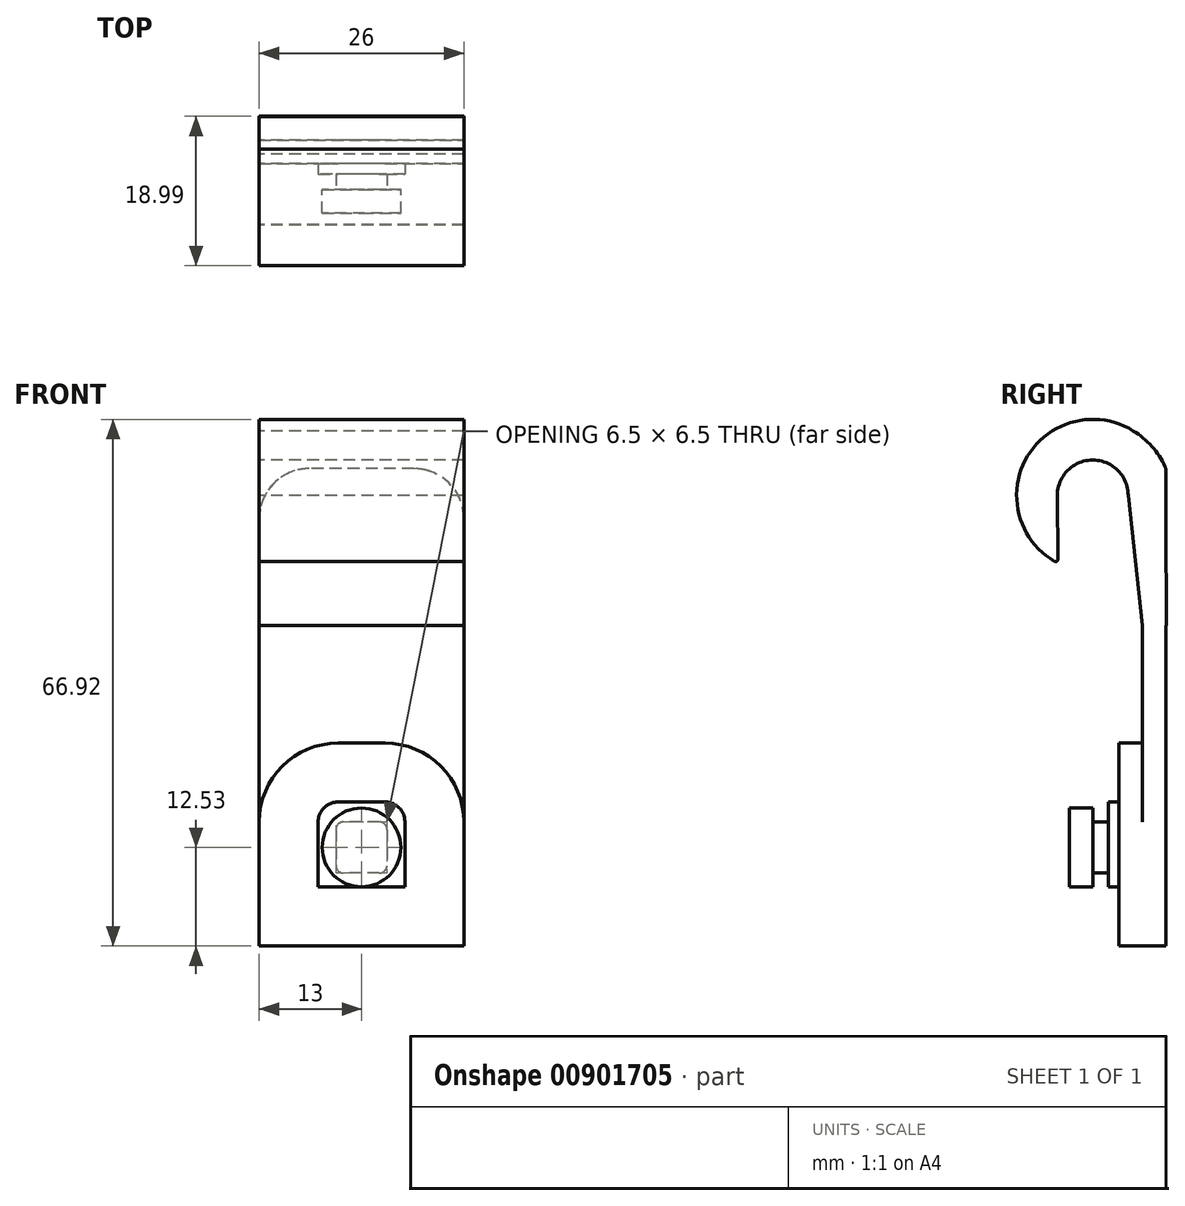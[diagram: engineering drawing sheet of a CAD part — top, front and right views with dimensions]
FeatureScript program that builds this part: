
annotation { "Feature Type Name" : "Feature", "Feature Type Description" : "" }
export const myFeature = defineFeature(function(context is Context, id is Id, definition is map)
    precondition{}
    {
        {
            var Q0;
            Q0=qCreatedBy(makeId("Front.planeOp"),FACE);
            var sketch = newSketch(context, id + "F0", { "sketchPlane" : qUnion([Q0])});
            skCircle(sketch, "E0", {"center": v(0, 0) * mm, "radius": 5 * mm});
            skSolve(sketch);
        }
        {
            var Q0;
            Q0 = qSketchRegion(id + "F0", true);
            extrude(context, id + "F1", {"entities" : qUnion([Q0]), "depth" : 3 * mm, "offsetDistance" : 25.4 * mm});
        }
        {
            var Q0;
            Q0=qCreatedBy(makeId("Front.planeOp"),FACE);
            var sketch = newSketch(context, id + "F2", { "sketchPlane" : qUnion([Q0])});
            skLineSegment(sketch, "E1.bottom", {"start": v(2.25, 3.25) * mm, "end": v(-2.25, 3.25) * mm});
            skLineSegment(sketch, "E1.top", {"start": v(2.25, -3.25) * mm, "end": v(-2.25, -3.25) * mm});
            skLineSegment(sketch, "E1.left", {"start": v(3.25, 2.25) * mm, "end": v(3.25, -2.25) * mm});
            skLineSegment(sketch, "E1.right", {"start": v(-3.25, 2.25) * mm, "end": v(-3.25, -2.25) * mm});
            skPoint(sketch, "E1.middle", {"position": v(0, 0) * mm});
            skArc(sketch, "E2", {"start": v(-2.25, 3.25) * mm, "mid": v(-2.96, 2.96) * mm, "end": v(-3.25, 2.25) * mm});
            skArc(sketch, "E3.MirrorCS", {"start": v(2.25, 3.25) * mm, "mid": v(2.96, 2.96) * mm, "end": v(3.25, 2.25) * mm});
            skArc(sketch, "E4.MirrorCS", {"start": v(-2.25, -3.25) * mm, "mid": v(-2.96, -2.96) * mm, "end": v(-3.25, -2.25) * mm});
            skArc(sketch, "E5.MirrorCS", {"start": v(2.25, -3.25) * mm, "mid": v(2.96, -2.96) * mm, "end": v(3.25, -2.25) * mm});
            skPoint(sketch, "E6.orphan", {"position": v(-3.25, 3.25) * mm});
            skPoint(sketch, "E7.orphan", {"position": v(3.25, 3.25) * mm});
            skPoint(sketch, "E8.orphan", {"position": v(3.25, -3.25) * mm});
            skPoint(sketch, "E9.orphan", {"position": v(-3.25, -3.25) * mm});
            skSolve(sketch);
        }
        {
            var Q0;
            Q0 = qSketchRegion(id + "F2", true);
            extrude(context, id + "F3", {"entities" : qUnion([Q0]), "operationType" : NewBodyOperationType.ADD, "oppositeDirection" : true, "depth" : 2 * mm, "offsetDistance" : 25.4 * mm});
        }
        {
            var Q0;
            Q0=qCreatedBy(makeId("Front.planeOp"),FACE);
            var sketch = newSketch(context, id + "F4", { "sketchPlane" : qUnion([Q0])});
            skLineSegment(sketch, "E10", {"start": v(0, 0) * mm, "end": v(0, -5.03) * mm});
            skPoint(sketch, "E10.endSnap0", {"position": v(0, -3.25) * mm});
            skLineSegment(sketch, "E11", {"start": v(0, -5.03) * mm, "end": v(-5.5, -5.03) * mm});
            skLineSegment(sketch, "E12", {"start": v(-5.5, -5.03) * mm, "end": v(-5.5, 3.25) * mm});
            skLineSegment(sketch, "E13", {"start": v(0, 3.25) * mm, "end": v(0, 5.75) * mm});
            skLineSegment(sketch, "E14", {"start": v(0, 5.75) * mm, "end": v(-3, 5.75) * mm});
            skLineSegment(sketch, "E15", {"start": v(0, 5.75) * mm, "end": v(3, 5.75) * mm});
            skLineSegment(sketch, "E16", {"start": v(5.5, 3.25) * mm, "end": v(5.5, -5.03) * mm});
            skLineSegment(sketch, "E17", {"start": v(5.5, -5.03) * mm, "end": v(0, -5.03) * mm});
            skLineSegment(sketch, "E18", {"start": v(5.5, 5.75) * mm, "end": v(3, 5.75) * mm});
            skArc(sketch, "E19", {"start": v(5.5, 3.25) * mm, "mid": v(4.77, 5.02) * mm, "end": v(3, 5.75) * mm});
            skArc(sketch, "E20.MirrorCS", {"start": v(-5.5, 3.25) * mm, "mid": v(-4.77, 5.02) * mm, "end": v(-3, 5.75) * mm});
            skSolve(sketch);
        }
        {
            var Q0;
            Q0=makeQuery(id+"F3.opExtrude","CAP_FACE",FACE,{"disambiguationData":[OSD([sQuery(id+"F2.wireOp",EDGE,"E1.bottom"),sQuery(id+"F2.wireOp",EDGE,"E1.top"),sQuery(id+"F2.wireOp",EDGE,"E1.left"),sQuery(id+"F2.wireOp",EDGE,"E1.right"),sQuery(id+"F2.wireOp",EDGE,"E2"),sQuery(id+"F2.wireOp",EDGE,"E3.MirrorCS"),sQuery(id+"F2.wireOp",EDGE,"E4.MirrorCS"),sQuery(id+"F2.wireOp",EDGE,"E5.MirrorCS")])],"isStart":false});
            var sketch = newSketch(context, id + "F5", { "sketchPlane" : qUnion([Q0])});
            skLineSegment(sketch, "E21", {"start": v(-3.02, 5.76) * mm, "end": v(3.01, 5.76) * mm});
            skLineSegment(sketch, "E22", {"start": v(-5.5, 3.28) * mm, "end": v(-5.5, -5.03) * mm});
            skLineSegment(sketch, "E23", {"start": v(-5.5, -5.03) * mm, "end": v(5.5, -5.03) * mm});
            skLineSegment(sketch, "E24", {"start": v(5.5, -5.03) * mm, "end": v(5.5, 3.25) * mm});
            skArc(sketch, "E25", {"start": v(-5.5, 3.28) * mm, "mid": v(-4.78, 5.04) * mm, "end": v(-3.02, 5.76) * mm});
            skArc(sketch, "E26", {"start": v(3.01, 5.76) * mm, "mid": v(4.78, 5.03) * mm, "end": v(5.5, 3.25) * mm});
            skSolve(sketch);
        }
        {
            var Q0;
            Q0 = qSketchRegion(id + "F5", true);
            extrude(context, id + "F6", {"entities" : qUnion([Q0]), "operationType" : NewBodyOperationType.ADD, "depth" : 1.3 * mm, "offsetDistance" : 25.4 * mm});
        }
        {
            var Q0;
            Q0=makeQuery(id+"F6.opExtrude","CAP_FACE",FACE,{"disambiguationData":[OSD([sQuery(id+"F5.wireOp",EDGE,"E21"),sQuery(id+"F5.wireOp",EDGE,"E22"),sQuery(id+"F5.wireOp",EDGE,"E23"),sQuery(id+"F5.wireOp",EDGE,"E24"),sQuery(id+"F5.wireOp",EDGE,"E25"),sQuery(id+"F5.wireOp",EDGE,"E26")])],"isStart":false});
            var sketch = newSketch(context, id + "F7", { "sketchPlane" : qUnion([Q0])});
            skLineSegment(sketch, "E27.0", {"start": v(0, 13.25) * mm, "end": v(3, 13.25) * mm});
            skArc(sketch, "E27.1", {"start": v(13, 3.25) * mm, "mid": v(10.07, 10.32) * mm, "end": v(3, 13.25) * mm});
            skLineSegment(sketch, "E27.2", {"start": v(0, 13.25) * mm, "end": v(-3, 13.25) * mm});
            skLineSegment(sketch, "E27.3", {"start": v(13, -12.53) * mm, "end": v(13, 3.25) * mm});
            skArc(sketch, "E27.4", {"start": v(-13, 3.25) * mm, "mid": v(-10.07, 10.32) * mm, "end": v(-3, 13.25) * mm});
            skLineSegment(sketch, "E27.5", {"start": v(-13, 3.25) * mm, "end": v(-13, -12.53) * mm});
            skLineSegment(sketch, "E27.6", {"start": v(-13, -12.53) * mm, "end": v(0, -12.53) * mm});
            skLineSegment(sketch, "E27.7", {"start": v(0, -12.53) * mm, "end": v(13, -12.53) * mm});
            skSolve(sketch);
        }
        {
            var Q0;
            Q0 = qSketchRegion(id + "F7", true);
            extrude(context, id + "F8", {"entities" : qUnion([Q0]), "operationType" : NewBodyOperationType.ADD, "depth" : 3 * mm, "offsetDistance" : 25.4 * mm});
        }
        {
            var Q0;
            Q0=makeQuery(id+"F8.opExtrude","CAP_FACE",FACE,{"disambiguationData":[OSD([sQuery(id+"F7.wireOp",EDGE,"E27.0"),sQuery(id+"F7.wireOp",EDGE,"E27.1"),sQuery(id+"F7.wireOp",EDGE,"E27.2"),sQuery(id+"F7.wireOp",EDGE,"E27.3"),sQuery(id+"F7.wireOp",EDGE,"E27.4"),sQuery(id+"F7.wireOp",EDGE,"E27.5"),sQuery(id+"F7.wireOp",EDGE,"E27.6"),sQuery(id+"F7.wireOp",EDGE,"E27.7")])],"isStart":false});
            var sketch = newSketch(context, id + "F9", { "sketchPlane" : qUnion([Q0])});
            skLineSegment(sketch, "E28", {"start": v(-13, -12.53) * mm, "end": v(-13, 41.78) * mm});
            skLineSegment(sketch, "E29", {"start": v(-6.65, 48.13) * mm, "end": v(6.65, 48.13) * mm});
            skPoint(sketch, "E29.endSnap0", {"position": v(13, -4.64) * mm});
            skLineSegment(sketch, "E30", {"start": v(13, 41.78) * mm, "end": v(13, -12.53) * mm});
            skLineSegment(sketch, "E31", {"start": v(13, -12.53) * mm, "end": v(-13, -12.53) * mm});
            skPoint(sketch, "E32.visualSharp", {"position": v(-13, 48.13) * mm});
            skArc(sketch, "E32.filletArc", {"start": v(-6.65, 48.13) * mm, "mid": v(-11.14, 46.27) * mm, "end": v(-13, 41.78) * mm});
            skPoint(sketch, "E33.visualSharp", {"position": v(13, 48.13) * mm});
            skArc(sketch, "E33.filletArc", {"start": v(13, 41.78) * mm, "mid": v(11.14, 46.27) * mm, "end": v(6.65, 48.13) * mm});
            skSolve(sketch);
        }
        {
            var Q0;
            Q0 = qSketchRegion(id + "F9", true);
            extrude(context, id + "F10", {"entities" : qUnion([Q0]), "operationType" : NewBodyOperationType.ADD, "depth" : 3 * mm, "offsetDistance" : 25.4 * mm});
        }
        {
            var Q0;
            Q0=qCreatedBy(makeId("Right.planeOp"),FACE);
            var sketch = newSketch(context, id + "F11", { "sketchPlane" : qUnion([Q0])});
            skArc(sketch, "E34", {"start": v(4.5, 44.72) * mm, "mid": v(-0.01, 49.22) * mm, "end": v(-4.5, 44.69) * mm});
            skArc(sketch, "E35", {"start": v(5.12, 52.92) * mm, "mid": v(-8.29, 49.7) * mm, "end": v(-4.86, 36.35) * mm});
            skLineSegment(sketch, "E36", {"start": v(-4.5, 44.69) * mm, "end": v(-4.45, 36.59) * mm});
            skArc(sketch, "E37", {"start": v(9.18, 48.38) * mm, "mid": v(5.46, 52.71) * mm, "end": v(0, 54.39) * mm});
            skLineSegment(sketch, "E38", {"start": v(4.5, 44.72) * mm, "end": v(6.3, 28.22) * mm});
            skLineSegment(sketch, "E39", {"start": v(6.3, 28.22) * mm, "end": v(9.32, 28.22) * mm});
            skLineSegment(sketch, "E40", {"start": v(9.32, 28.22) * mm, "end": v(9.3, 47.86) * mm});
            skPoint(sketch, "E41.visualSharp", {"position": v(-4.45, 36.13) * mm});
            skArc(sketch, "E41.filletArc", {"start": v(-4.86, 36.35) * mm, "mid": v(-4.59, 36.35) * mm, "end": v(-4.45, 36.59) * mm});
            skPoint(sketch, "E42.visualSharp", {"position": v(9.3, 48.12) * mm});
            skArc(sketch, "E42.filletArc", {"start": v(9.3, 47.86) * mm, "mid": v(9.26, 48.12) * mm, "end": v(9.18, 48.38) * mm});
            skSolve(sketch);
        }
        {
            var Q0;
            Q0 = qSketchRegion(id + "F11", true);
            extrude(context, id + "F12", {"entities" : qUnion([Q0]), "operationType" : NewBodyOperationType.ADD, "endBound" : BoundingType.SYMMETRIC, "depth" : 26 * mm, "offsetDistance" : 25.4 * mm});
        }
    });
